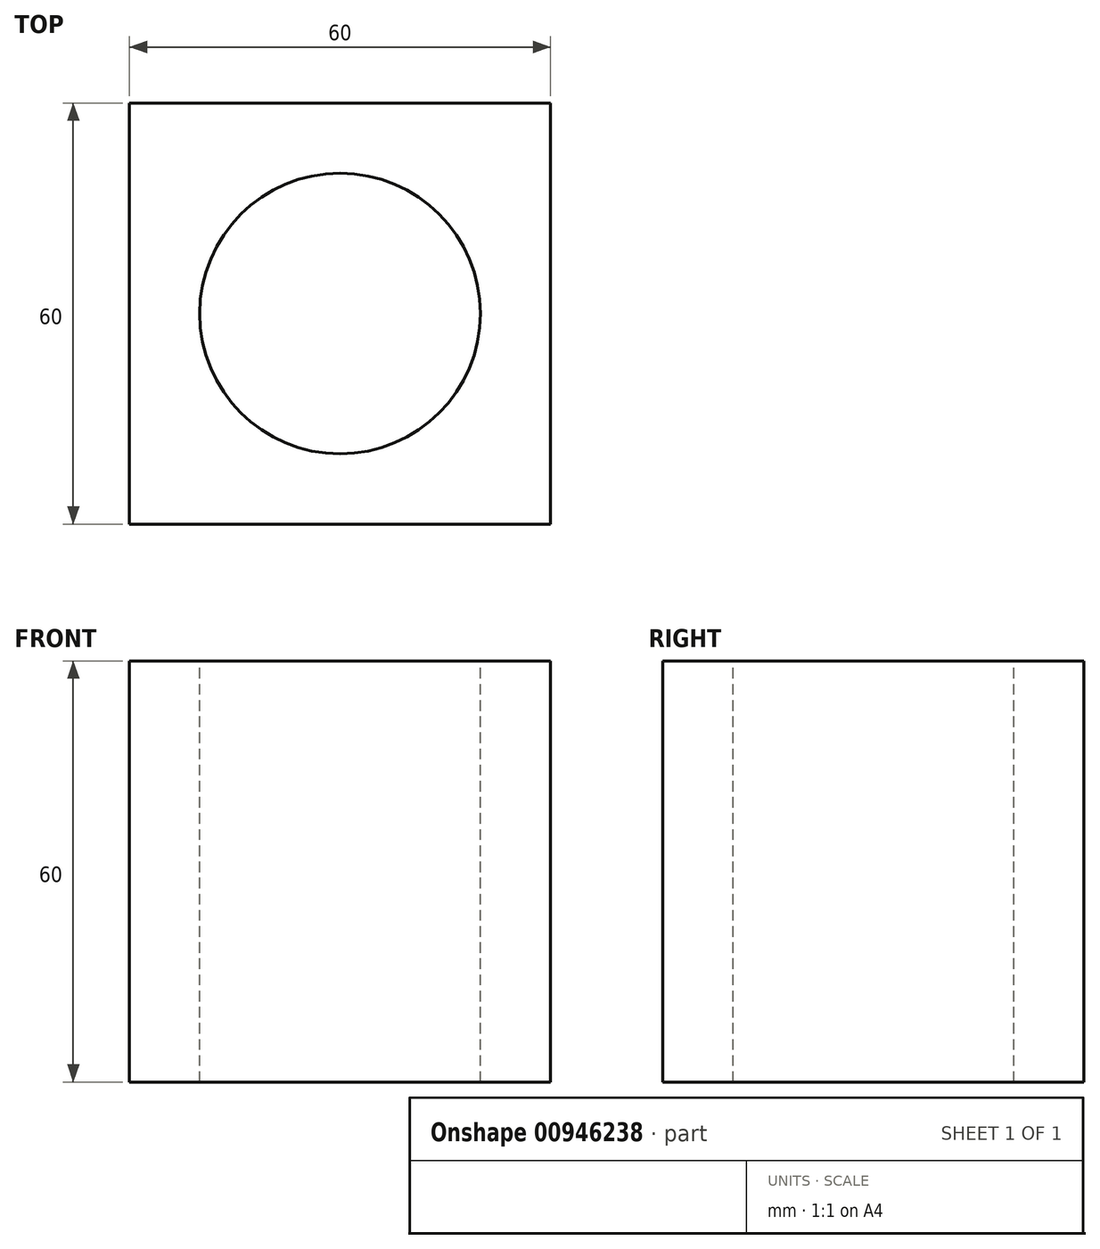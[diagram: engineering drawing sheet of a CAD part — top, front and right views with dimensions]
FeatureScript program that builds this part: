
annotation { "Feature Type Name" : "Feature", "Feature Type Description" : "" }
export const myFeature = defineFeature(function(context is Context, id is Id, definition is map)
    precondition{}
    {
        {
            var Q0;
            Q0=qCreatedBy(makeId("Top.planeOp"),FACE);
            var sketch = newSketch(context, id + "F0", { "sketchPlane" : qUnion([Q0])});
            skLineSegment(sketch, "E0.bottom", {"start": v(30, 30) * mm, "end": v(-30, 30) * mm});
            skLineSegment(sketch, "E0.top", {"start": v(30, -30) * mm, "end": v(-30, -30) * mm});
            skLineSegment(sketch, "E0.left", {"start": v(30, 30) * mm, "end": v(30, -30) * mm});
            skLineSegment(sketch, "E0.right", {"start": v(-30, 30) * mm, "end": v(-30, -30) * mm});
            skPoint(sketch, "E0.middle", {"position": v(0, 0) * mm});
            skSolve(sketch);
        }
        {
            var Q0;
            Q0 = qSketchRegion(id + "F0", true);
            extrude(context, id + "F1", {"entities" : qUnion([Q0]), "depth" : 60 * mm, "offsetDistance" : 25 * mm});
        }
        {
            var Q0;
            Q0=makeQuery(id+"F1.opExtrude","CAP_FACE",FACE,{"disambiguationData":[OSD([sQuery(id+"F0.wireOp",EDGE,"E0.bottom"),sQuery(id+"F0.wireOp",EDGE,"E0.top"),sQuery(id+"F0.wireOp",EDGE,"E0.left"),sQuery(id+"F0.wireOp",EDGE,"E0.right")])],"isStart":false});
            var sketch = newSketch(context, id + "F2", { "sketchPlane" : qUnion([Q0])});
            skCircle(sketch, "E1", {"center": v(0, 0) * mm, "radius": 20 * mm});
            skSolve(sketch);
        }
        {
            var Q0;
            Q0=makeQuery(id+"F2.imprint","IMPRINT",FACE,{"disambiguationData":[TD([[makeQuery(id+"F2.imprint","IMPRINT",EDGE,{"derivedFrom":sQuery(id+"F2.wireOp",EDGE,"E1")}),1.0]])]});
            extrude(context, id + "F3", {"entities" : qUnion([Q0]), "operationType" : NewBodyOperationType.REMOVE, "endBound" : BoundingType.THROUGH_ALL, "oppositeDirection" : true, "depth" : 25 * mm, "offsetDistance" : 25 * mm});
        }
    });
